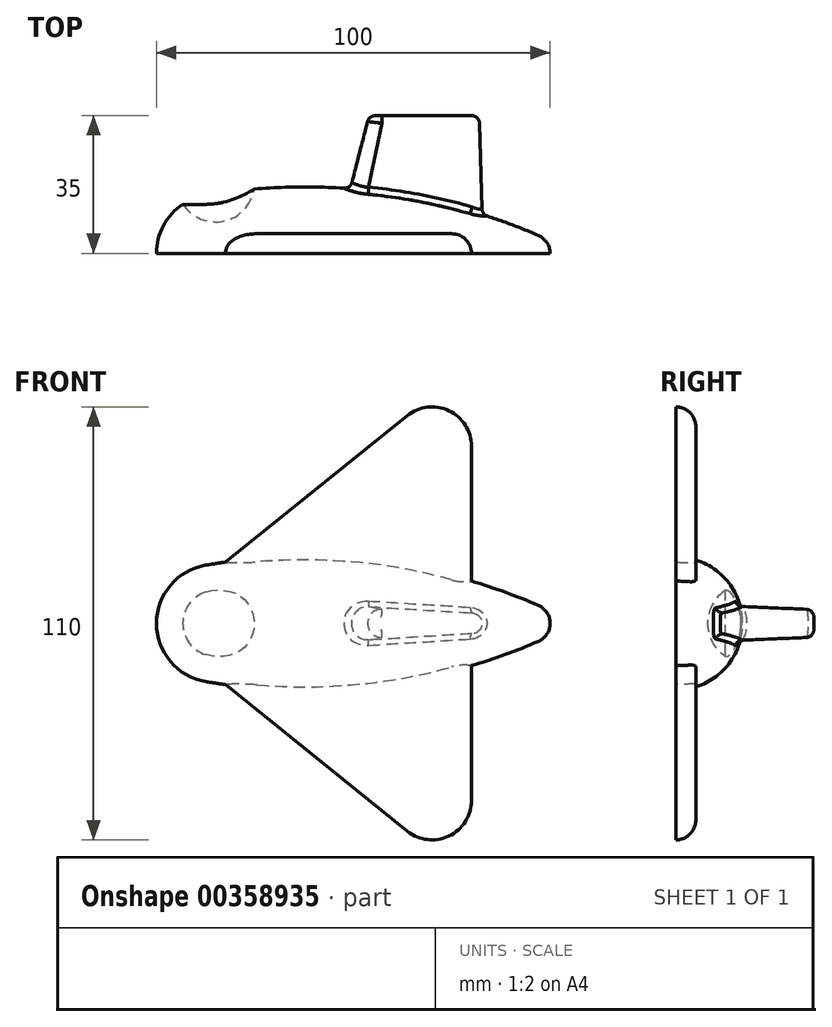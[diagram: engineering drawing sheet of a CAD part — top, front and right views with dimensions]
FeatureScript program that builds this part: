
annotation { "Feature Type Name" : "Feature", "Feature Type Description" : "" }
export const myFeature = defineFeature(function(context is Context, id is Id, definition is map)
    precondition{}
    {
        {
            var Q0;
            Q0=qCreatedBy(makeId("Top.planeOp"),FACE);
            var sketch = newSketch(context, id + "F0", { "sketchPlane" : qUnion([Q0])});
            skArc(sketch, "E0", {"start": v(-2.5, 14.8) * mm, "mid": v(-11.46, 9.68) * mm, "end": v(-15, 0) * mm});
            skArc(sketch, "E1", {"start": v(85, 0) * mm, "mid": v(84.18, 2.75) * mm, "end": v(81.98, 4.6) * mm});
            skArc(sketch, "E2", {"start": v(81.98, 4.6) * mm, "mid": v(40.48, 15.8) * mm, "end": v(-2.5, 14.8) * mm});
            skLineSegment(sketch, "E3", {"start": v(-15, 0) * mm, "end": v(85, 0) * mm});
            skSolve(sketch);
        }
        {
            var Q0;
            Q0 = qSketchRegion(id + "F0", true);
            var Q1;
            Q1=sQuery(id+"F0.wireOp",EDGE,"E3");
            revolve(context, id + "F1", {"entities" : qUnion([Q0]), "axis" : qUnion([Q1]), "revolveType" : RevolveType.SYMMETRIC, "angle" : 180 * degree});
        }
        {
            var Q0;
            Q0=qCreatedBy(makeId("Top.planeOp"),FACE);
            var sketch = newSketch(context, id + "F2", { "sketchPlane" : qUnion([Q0])});
            skArc(sketch, "E4", {"start": v(-10, 18) * mm, "mid": v(0, 8) * mm, "end": v(10, 18) * mm});
            skLineSegment(sketch, "E5", {"start": v(-10, 18) * mm, "end": v(10, 18) * mm});
            skSolve(sketch);
        }
        {
            var Q0;
            Q0=makeQuery(id+"F2.imprint","IMPRINT",FACE,{"disambiguationData":[TD([[makeQuery(id+"F2.imprint","IMPRINT",EDGE,{"derivedFrom":sQuery(id+"F2.wireOp",EDGE,"E4")}),1.0]])]});
            var Q1;
            Q1=sQuery(id+"F2.wireOp",EDGE,"E5");
            revolve(context, id + "F3", {"operationType" : NewBodyOperationType.REMOVE, "entities" : qUnion([Q0]), "axis" : qUnion([Q1]), "revolveType" : RevolveType.FULL, "oppositeDirection" : true});
        }
        {
            var Q0;
            Q0=qCreatedBy(makeId("Front.planeOp"),FACE);
            var sketch = newSketch(context, id + "F4", { "sketchPlane" : qUnion([Q0])});
            skArc(sketch, "E6", {"start": v(35.33, 4.99) * mm, "mid": v(30, 0) * mm, "end": v(35.33, -4.99) * mm});
            skArc(sketch, "E7", {"start": v(65.2, -3) * mm, "mid": v(68, 0) * mm, "end": v(65.2, 3) * mm});
            skLineSegment(sketch, "E8", {"start": v(35.33, 4.99) * mm, "end": v(65.2, 3) * mm});
            skLineSegment(sketch, "E9.MirrorCS", {"start": v(35.33, -4.99) * mm, "end": v(65.2, -3) * mm});
            skSolve(sketch);
        }
        {
            var Q0;
            Q0=qCreatedBy(makeId("Front.planeOp"),FACE);
            cPlane(context, id + "F5", {"entities" : qUnion([Q0]), "cplaneType" : CPlaneType.OFFSET, "offset" : 35 * mm, "oppositeDirection" : true, "width" : 150 * mm, "height" : 150 * mm});
        }
        {
            var Q0;
            Q0=qCreatedBy(id+"F5.planeOp",FACE);
            var sketch = newSketch(context, id + "F6", { "sketchPlane" : qUnion([Q0])});
            skArc(sketch, "E10", {"start": v(42.73, 3.5) * mm, "mid": v(39, 0) * mm, "end": v(42.73, -3.5) * mm});
            skArc(sketch, "E11", {"start": v(65.13, -2) * mm, "mid": v(67, 0) * mm, "end": v(65.13, 2) * mm});
            skLineSegment(sketch, "E12", {"start": v(42.73, 3.5) * mm, "end": v(65.13, 2) * mm});
            skLineSegment(sketch, "E13.MirrorCS", {"start": v(42.73, -3.5) * mm, "end": v(65.13, -2) * mm});
            skSolve(sketch);
        }
        {
            var Q1;
            Q1 = qSketchRegion(id + "F4", true);
            var Q2;
            Q2 = qSketchRegion(id + "F6", true);
            loft(context, id + "F7", {"operationType" : NewBodyOperationType.ADD, "sheetProfilesArray" : [{ "sheetProfileEntities" : qUnion([Q1]) }, { "sheetProfileEntities" : qUnion([Q2]) }]});
        }
        {
            var Q0;
            Q0=makeQuery(id+"F7.opLoft","MID_CAP_EDGE",EDGE,{"disambiguationData":[OSD([sQuery(id+"F6.wireOp",EDGE,"E10"),sQuery(id+"F6.wireOp",EDGE,"E12"),sQuery(id+"F6.wireOp",EDGE,"E13.MirrorCS")])],"capPos":1.0});
            var Q1;
            Q1=makeQuery(id+"F7.opLoft","MID_CAP_EDGE",EDGE,{"disambiguationData":[OSD([sQuery(id+"F6.wireOp",EDGE,"E10"),sQuery(id+"F6.wireOp",EDGE,"E11"),sQuery(id+"F6.wireOp",EDGE,"E12")])],"capPos":1.0});
            var Q2;
            Q2=makeQuery(id+"F7.opLoft","MID_CAP_EDGE",EDGE,{"disambiguationData":[OSD([sQuery(id+"F6.wireOp",EDGE,"E10"),sQuery(id+"F6.wireOp",EDGE,"E11"),sQuery(id+"F6.wireOp",EDGE,"E13.MirrorCS")])],"capPos":1.0});
            fillet(context, id + "F8", {"entities" : qUnion([Q0, Q1, Q2]), "radius" : 2 * mm, "tangentPropagation" : true, "allowEdgeOverflow" : false});
        }
        {
            var Q0;
            Q0=makeQuery(id+"F7.boolean.opBoolean","INTERSECT",EDGE,{"derivedFrom":[makeQuery(id+"F1.opRevolve","SWEPT_FACE",FACE,{"disambiguationData":[OSD([sQuery(id+"F0.wireOp",EDGE,"E2")])]}),makeQuery(id+"F7.opLoft","SWEPT_FACE",FACE,{"disambiguationData":[OSD([sQuery(id+"F4.wireOp",EDGE,"E6"),sQuery(id+"F4.wireOp",EDGE,"E8"),sQuery(id+"F4.wireOp",EDGE,"E9.MirrorCS"),sQuery(id+"F6.wireOp",EDGE,"E10"),sQuery(id+"F6.wireOp",EDGE,"E12"),sQuery(id+"F6.wireOp",EDGE,"E13.MirrorCS")])]})]});
            var Q1;
            Q1=makeQuery(id+"F7.boolean.opBoolean","INTERSECT",EDGE,{"derivedFrom":[makeQuery(id+"F1.opRevolve","SWEPT_FACE",FACE,{"disambiguationData":[OSD([sQuery(id+"F0.wireOp",EDGE,"E2")])]}),makeQuery(id+"F7.opLoft","SWEPT_FACE",FACE,{"disambiguationData":[OSD([sQuery(id+"F4.wireOp",EDGE,"E6"),sQuery(id+"F4.wireOp",EDGE,"E7"),sQuery(id+"F4.wireOp",EDGE,"E8"),sQuery(id+"F6.wireOp",EDGE,"E10"),sQuery(id+"F6.wireOp",EDGE,"E11"),sQuery(id+"F6.wireOp",EDGE,"E12")])]})]});
            var Q2;
            Q2=makeQuery(id+"F7.boolean.opBoolean","INTERSECT",EDGE,{"derivedFrom":[makeQuery(id+"F1.opRevolve","SWEPT_FACE",FACE,{"disambiguationData":[OSD([sQuery(id+"F0.wireOp",EDGE,"E2")])]}),makeQuery(id+"F7.opLoft","SWEPT_FACE",FACE,{"disambiguationData":[OSD([sQuery(id+"F4.wireOp",EDGE,"E6"),sQuery(id+"F4.wireOp",EDGE,"E7"),sQuery(id+"F4.wireOp",EDGE,"E9.MirrorCS"),sQuery(id+"F6.wireOp",EDGE,"E10"),sQuery(id+"F6.wireOp",EDGE,"E11"),sQuery(id+"F6.wireOp",EDGE,"E13.MirrorCS")])]})]});
            var Q3;
            Q3=makeQuery(id+"F7.boolean.opBoolean","INTERSECT",EDGE,{"derivedFrom":[makeQuery(id+"F1.opRevolve","SWEPT_FACE",FACE,{"disambiguationData":[OSD([sQuery(id+"F0.wireOp",EDGE,"E2")])]}),makeQuery(id+"F7.opLoft","SWEPT_FACE",FACE,{"disambiguationData":[OSD([sQuery(id+"F4.wireOp",EDGE,"E7"),sQuery(id+"F4.wireOp",EDGE,"E8"),sQuery(id+"F4.wireOp",EDGE,"E9.MirrorCS"),sQuery(id+"F6.wireOp",EDGE,"E11"),sQuery(id+"F6.wireOp",EDGE,"E12"),sQuery(id+"F6.wireOp",EDGE,"E13.MirrorCS")])]})]});
            fillet(context, id + "F9", {"entities" : qUnion([Q0, Q1, Q2, Q3]), "radius" : 2 * mm, "tangentPropagation" : true, "allowEdgeOverflow" : false});
        }
        {
            var Q0;
            Q0=qCreatedBy(makeId("Front.planeOp"),FACE);
            var sketch = newSketch(context, id + "F10", { "sketchPlane" : qUnion([Q0])});
            skLineSegment(sketch, "E14", {"start": v(2.5, -15.55) * mm, "end": v(48.73, -52.79) * mm});
            skLineSegment(sketch, "E15", {"start": v(65, -45) * mm, "end": v(65, -7.5) * mm});
            skArc(sketch, "E16.filletArc", {"start": v(48.73, -52.79) * mm, "mid": v(59.32, -54.02) * mm, "end": v(65, -45) * mm});
            skLineSegment(sketch, "E17", {"start": v(2.5, -15.55) * mm, "end": v(-1.37, -12.43) * mm});
            skLineSegment(sketch, "E18", {"start": v(-1.37, -12.43) * mm, "end": v(65, -7.5) * mm});
            skLineSegment(sketch, "E19.MirrorCS", {"start": v(2.5, 15.55) * mm, "end": v(48.73, 52.79) * mm});
            skLineSegment(sketch, "E20.MirrorCS", {"start": v(-1.37, 12.43) * mm, "end": v(65, 7.5) * mm});
            skLineSegment(sketch, "E21.MirrorCS", {"start": v(2.5, 15.55) * mm, "end": v(-1.37, 12.43) * mm});
            skLineSegment(sketch, "E22.MirrorCS", {"start": v(65, 45) * mm, "end": v(65, 7.5) * mm});
            skArc(sketch, "E23.MirrorCS", {"start": v(48.73, 52.79) * mm, "mid": v(59.32, 54.02) * mm, "end": v(65, 45) * mm});
            skSolve(sketch);
        }
        {
            var Q0;
            Q0 = qSketchRegion(id + "F10", true);
            extrude(context, id + "F11", {"entities" : qUnion([Q0]), "operationType" : NewBodyOperationType.ADD, "oppositeDirection" : true, "depth" : 5 * mm});
        }
        {
            var Q0;
            Q0=makeQuery(id+"F11.opExtrude","CAP_EDGE",EDGE,{"disambiguationData":[OSD([sQuery(id+"F10.wireOp",EDGE,"E19.MirrorCS"),sQuery(id+"F10.wireOp",EDGE,"E21.MirrorCS")])],"isStart":false});
            var Q1;
            Q1=makeQuery(id+"F11.opExtrude","CAP_EDGE",EDGE,{"disambiguationData":[OSD([sQuery(id+"F10.wireOp",EDGE,"E23.MirrorCS")])],"isStart":false});
            var Q2;
            Q2=makeQuery(id+"F11.opExtrude","CAP_EDGE",EDGE,{"disambiguationData":[OSD([sQuery(id+"F10.wireOp",EDGE,"E15")])],"isStart":false});
            fillet(context, id + "F12", {"entities" : qUnion([Q0, Q1, Q2]), "radius" : 5 * mm, "tangentPropagation" : true, "allowEdgeOverflow" : false});
        }
    });
